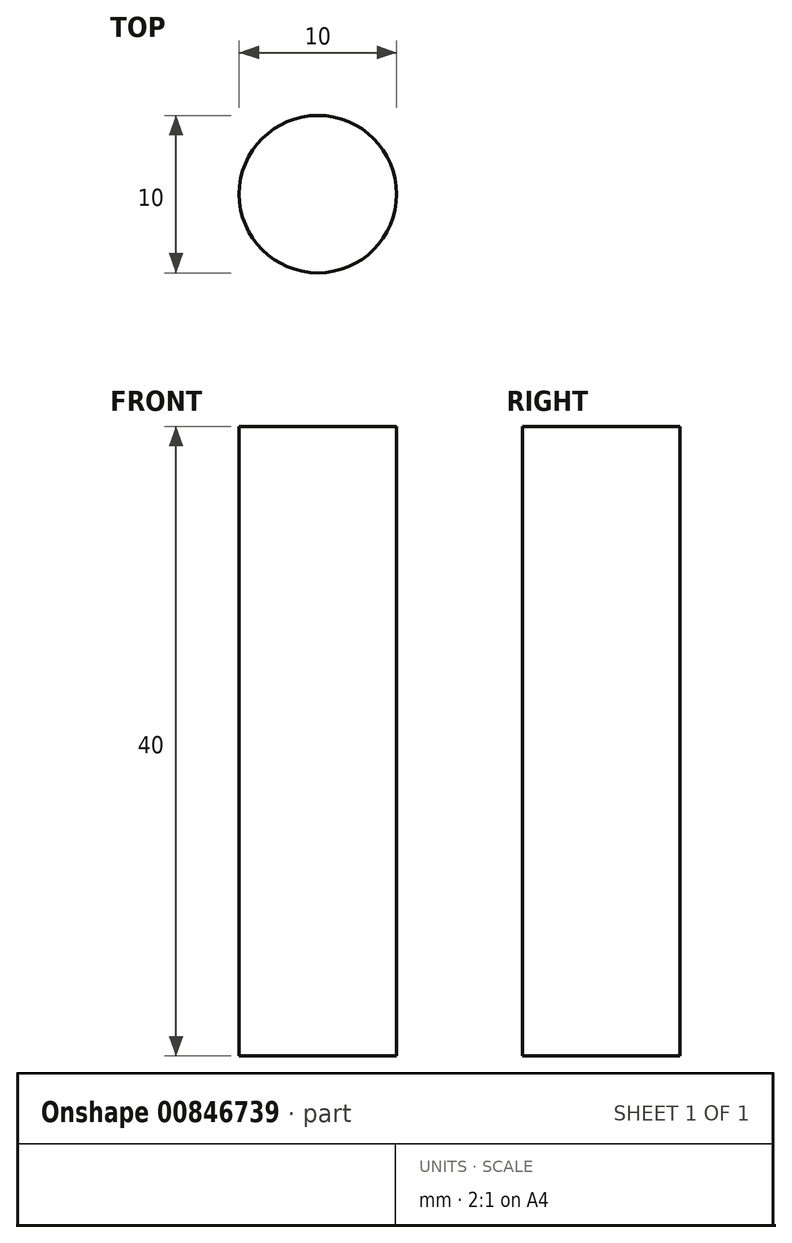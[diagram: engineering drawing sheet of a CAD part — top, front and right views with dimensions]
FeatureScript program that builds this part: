
annotation { "Feature Type Name" : "Feature", "Feature Type Description" : "" }
export const myFeature = defineFeature(function(context is Context, id is Id, definition is map)
    precondition{}
    {
        {
            var Q0;
            Q0=qCreatedBy(makeId("Top.planeOp"),FACE);
            var sketch = newSketch(context, id + "F0", { "sketchPlane" : qUnion([Q0])});
            skCircle(sketch, "E0", {"center": v(0, 0) * mm, "radius": 5 * mm});
            skSolve(sketch);
        }
        {
            var Q0;
            Q0 = qSketchRegion(id + "F0", true);
            extrude(context, id + "F1", {"entities" : qUnion([Q0]), "oppositeDirection" : true, "depth" : 40 * mm, "offsetDistance" : 25 * mm});
        }
    });
